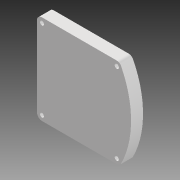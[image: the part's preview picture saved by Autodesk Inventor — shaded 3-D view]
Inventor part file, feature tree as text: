
AUTODESK INVENTOR PART (.ipt)
format: ipt  version: 2021 (Build 250183000, 183)  size: 137,216 bytes
history: native  units: in
note: dims shown in document units (in); Inventor stores cm internally (conversion verified against a paired STEP export)
features: reference x12, extrude x2, sketch x2, projected_geometry x1, other x1
ambient origin geometry x8: Origin, YZ Plane, XZ Plane, XY Plane, X Axis, Y Axis, Z Axis, Center Point
bodies: Solid1 (feature_tree)
feature tree (18):
  extrude  "Extrusion1"  Depth=0.1575in TaperAngle=0.0deg
  extrude  "Extrusion2"  [1 undecoded]
  sketch  "Sketch1"  dims[d0=0.315in d1=0.0in d2=0.1575in d3=0.0in]
  reference  "Reference1"
  reference  "Reference2"
  reference  "Reference3"
  reference  "Reference4"
  reference  "Reference5"
  reference  "Reference6"
  reference  "Reference7"
  reference  "Reference8"
  reference  "Reference9"
  reference  "Reference10"
  reference  "Reference11"
  reference  "Reference12"
  sketch  "Sketch2"
  projected_geometry  "Projected Loop1"
  other  "Impedance_Analyzer_V2.iam"
note: 1 required parameter value undecoded (feature->parameter linkage not recoverable at this tier; creation-order binding heuristic only, values carry confidence <= 0.55)
